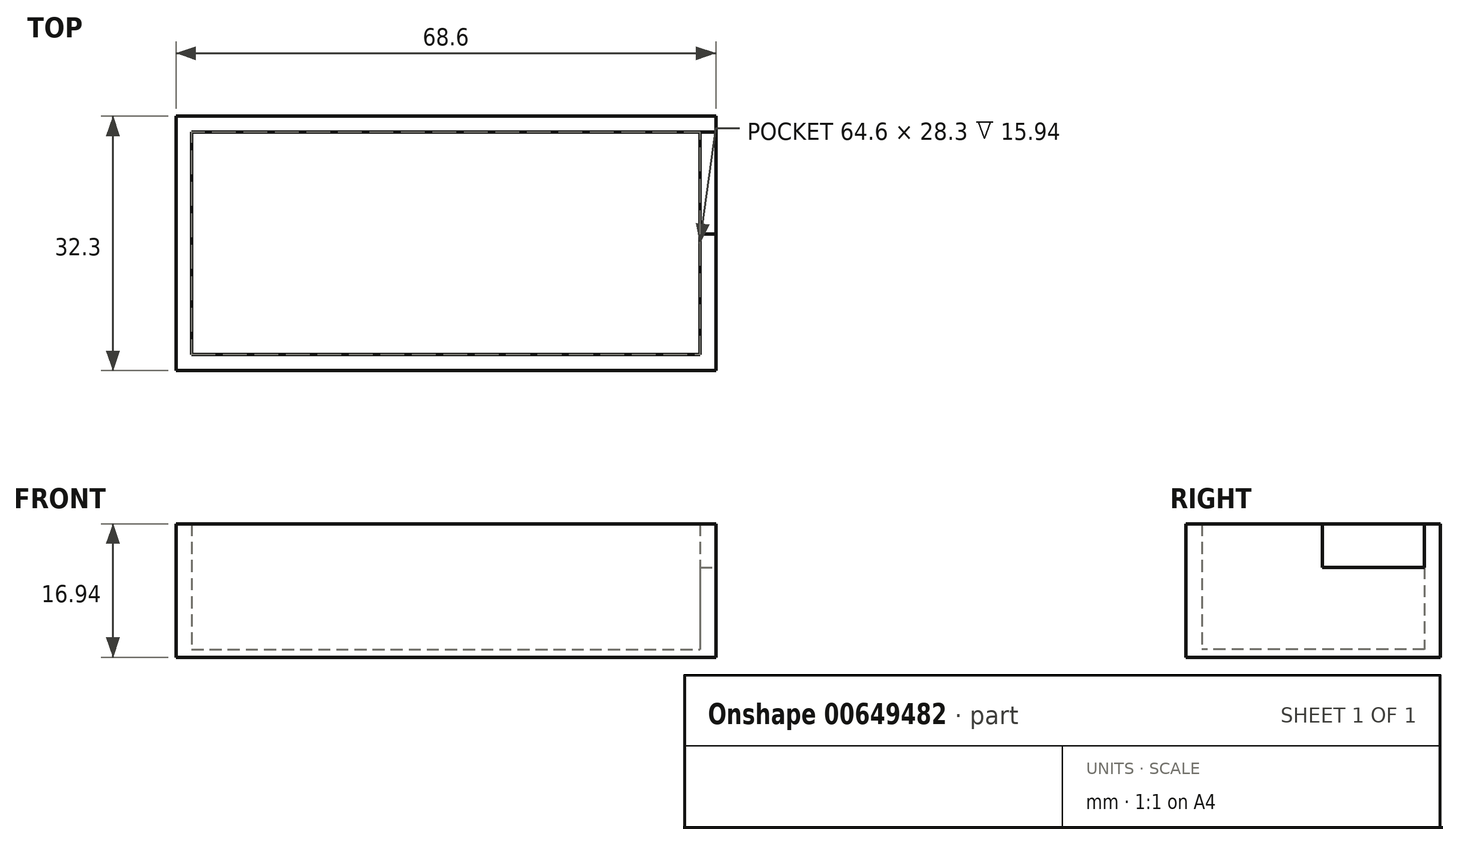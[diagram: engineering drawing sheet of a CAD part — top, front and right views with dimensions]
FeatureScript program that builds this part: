
annotation { "Feature Type Name" : "Feature", "Feature Type Description" : "" }
export const myFeature = defineFeature(function(context is Context, id is Id, definition is map)
    precondition{}
    {
        {
            var Q0;
            Q0=qCreatedBy(makeId("Top.planeOp"),FACE);
            var sketch = newSketch(context, id + "F0", { "sketchPlane" : qUnion([Q0])});
            skLineSegment(sketch, "E0.bottom", {"start": v(0, 0) * mm, "end": v(68.6, 0) * mm});
            skLineSegment(sketch, "E0.top", {"start": v(0, 32.3) * mm, "end": v(68.6, 32.3) * mm});
            skLineSegment(sketch, "E0.left", {"start": v(0, 0) * mm, "end": v(0, 32.3) * mm});
            skLineSegment(sketch, "E0.right", {"start": v(68.6, 0) * mm, "end": v(68.6, 32.3) * mm});
            skSolve(sketch);
        }
        {
            var Q0;
            Q0=makeQuery(id+"F0.imprint","IMPRINT",FACE,{"disambiguationData":[TD([[makeQuery(id+"F0.imprint","IMPRINT",EDGE,{"derivedFrom":sQuery(id+"F0.wireOp",EDGE,"E0.bottom")}),1.0]])]});
            extrude(context, id + "F1", {"entities" : qUnion([Q0]), "depth" : 1 * mm, "offsetDistance" : 25 * mm});
        }
        {
            var Q0;
            Q0=makeQuery(id+"F1.opExtrude","CAP_FACE",FACE,{"disambiguationData":[OSD([sQuery(id+"F0.wireOp",EDGE,"E0.bottom"),sQuery(id+"F0.wireOp",EDGE,"E0.top"),sQuery(id+"F0.wireOp",EDGE,"E0.left"),sQuery(id+"F0.wireOp",EDGE,"E0.right")])],"isStart":false});
            var sketch = newSketch(context, id + "F2", { "sketchPlane" : qUnion([Q0])});
            skLineSegment(sketch, "E1.bottom", {"start": v(0, 32.3) * mm, "end": v(68.6, 32.3) * mm});
            skLineSegment(sketch, "E1.top", {"start": v(0, 0) * mm, "end": v(68.6, 0) * mm});
            skLineSegment(sketch, "E1.left", {"start": v(0, 32.3) * mm, "end": v(0, 0) * mm});
            skLineSegment(sketch, "E1.right", {"start": v(68.6, 32.3) * mm, "end": v(68.6, 0) * mm});
            skLineSegment(sketch, "E2.bottom", {"start": v(2, 30.3) * mm, "end": v(66.6, 30.3) * mm});
            skLineSegment(sketch, "E2.top", {"start": v(2, 2) * mm, "end": v(66.6, 2) * mm});
            skLineSegment(sketch, "E2.left", {"start": v(2, 30.3) * mm, "end": v(2, 2) * mm});
            skLineSegment(sketch, "E2.right", {"start": v(66.6, 30.3) * mm, "end": v(66.6, 2) * mm});
            skSolve(sketch);
        }
        {
            var Q0;
            Q0=makeQuery(id+"F2.imprint","IMPRINT",FACE,{"disambiguationData":[TD([[makeQuery(id+"F2.imprint","IMPRINT",EDGE,{"derivedFrom":sQuery(id+"F2.wireOp",EDGE,"E1.bottom")}),-1.0]])]});
            extrude(context, id + "F3", {"entities" : qUnion([Q0]), "operationType" : NewBodyOperationType.ADD, "depth" : 15.94 * mm, "offsetDistance" : 25 * mm});
        }
        {
            var Q0;
            Q0=makeQuery(id+"F3.boolean.opBoolean","MERGE",FACE,{"derivedFrom":[makeQuery(id+"F1.opExtrude","SWEPT_FACE",FACE,{"disambiguationData":[OSD([sQuery(id+"F0.wireOp",EDGE,"E0.right")])]}),makeQuery(id+"F3.opExtrude","SWEPT_FACE",FACE,{"disambiguationData":[OSD([sQuery(id+"F2.wireOp",EDGE,"E1.right")])]})]});
            var sketch = newSketch(context, id + "F4", { "sketchPlane" : qUnion([Q0])});
            skLineSegment(sketch, "E3.bottom", {"start": v(17.3, 16.94) * mm, "end": v(30.3, 16.94) * mm});
            skLineSegment(sketch, "E3.top", {"start": v(17.3, 11.44) * mm, "end": v(30.3, 11.44) * mm});
            skLineSegment(sketch, "E3.left", {"start": v(17.3, 16.94) * mm, "end": v(17.3, 11.44) * mm});
            skLineSegment(sketch, "E3.right", {"start": v(30.3, 16.94) * mm, "end": v(30.3, 11.44) * mm});
            skSolve(sketch);
        }
        {
            var Q0;
            Q0=makeQuery(id+"F4.imprint","IMPRINT",FACE,{"disambiguationData":[TD([[makeQuery(id+"F4.imprint","IMPRINT",EDGE,{"derivedFrom":sQuery(id+"F4.wireOp",EDGE,"E3.bottom")}),-1.0]])]});
            extrude(context, id + "F5", {"entities" : qUnion([Q0]), "operationType" : NewBodyOperationType.REMOVE, "oppositeDirection" : true, "depth" : 25 * mm, "offsetDistance" : 25 * mm});
        }
    });
